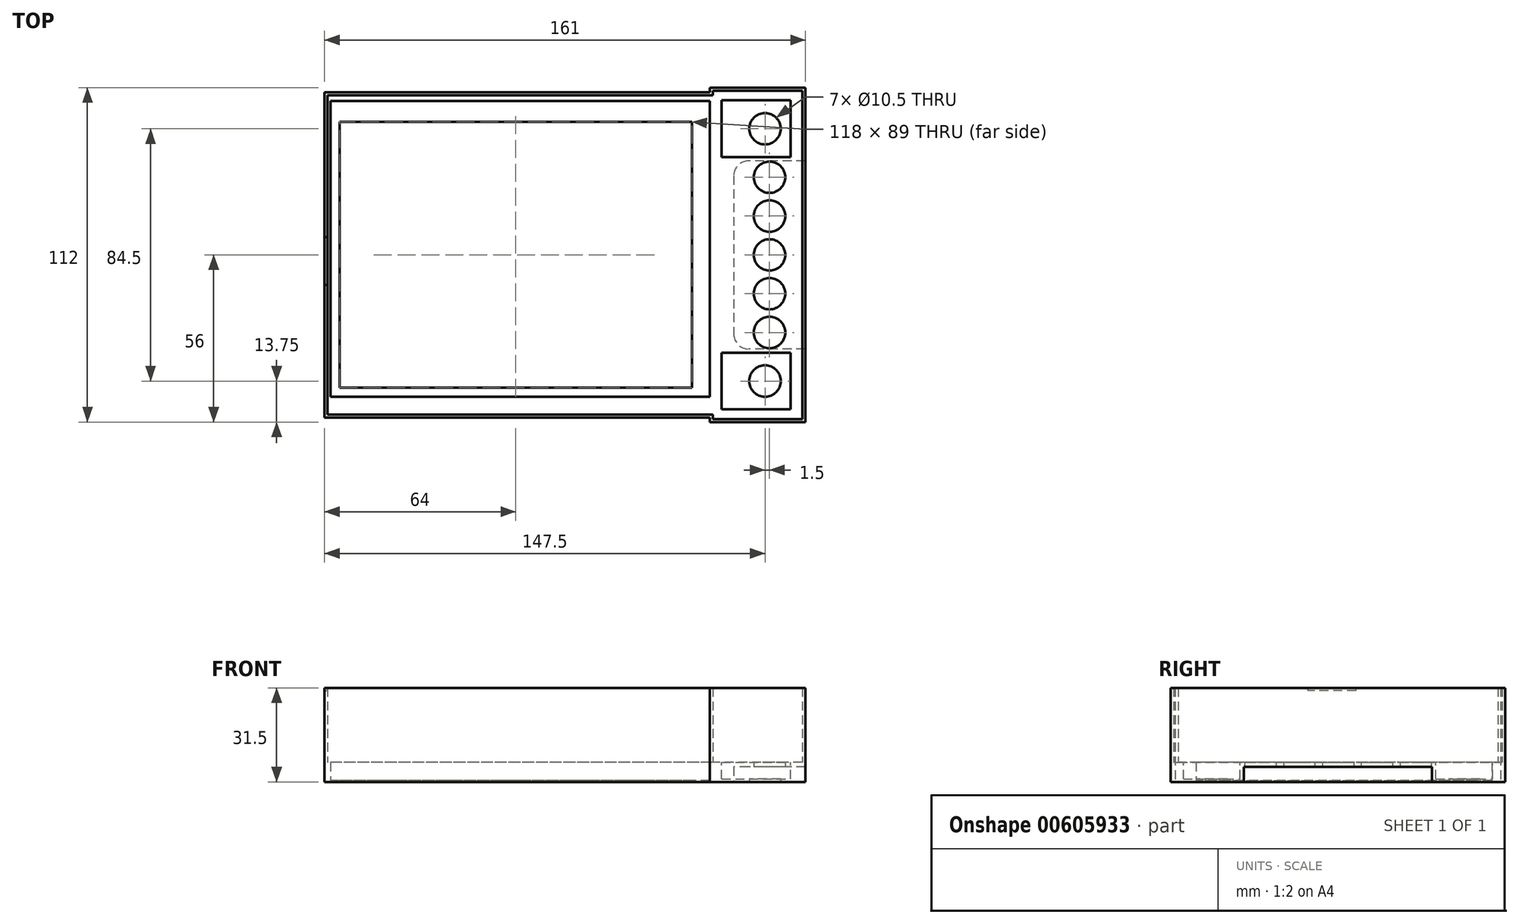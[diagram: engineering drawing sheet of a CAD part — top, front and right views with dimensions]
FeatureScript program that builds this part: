
annotation { "Feature Type Name" : "Feature", "Feature Type Description" : "" }
export const myFeature = defineFeature(function(context is Context, id is Id, definition is map)
    precondition{}
    {
        {
            var Q0;
            Q0=qCreatedBy(makeId("Top.planeOp"),FACE);
            var sketch = newSketch(context, id + "F0", { "sketchPlane" : qUnion([Q0])});
            skLineSegment(sketch, "E0.bottom", {"start": v(59, -44.5) * mm, "end": v(-59, -44.5) * mm});
            skLineSegment(sketch, "E0.top", {"start": v(59, 44.5) * mm, "end": v(-59, 44.5) * mm});
            skLineSegment(sketch, "E0.left", {"start": v(59, -44.5) * mm, "end": v(59, 44.5) * mm});
            skLineSegment(sketch, "E0.right", {"start": v(-59, -44.5) * mm, "end": v(-59, 44.5) * mm});
            skPoint(sketch, "E0.middle", {"position": v(0, 0) * mm});
            skLineSegment(sketch, "E1", {"start": v(65, 51.5) * mm, "end": v(-62, 51.5) * mm});
            skLineSegment(sketch, "E2", {"start": v(-62, 51.5) * mm, "end": v(-62, -47.5) * mm});
            skLineSegment(sketch, "E3", {"start": v(-62, -47.5) * mm, "end": v(65, -47.5) * mm});
            skLineSegment(sketch, "E4", {"start": v(65, 56) * mm, "end": v(97, 56) * mm});
            skLineSegment(sketch, "E5", {"start": v(97, 56) * mm, "end": v(97, -56) * mm});
            skLineSegment(sketch, "E6", {"start": v(97, -56) * mm, "end": v(65, -56) * mm});
            skLineSegment(sketch, "E7", {"start": v(65, 51.5) * mm, "end": v(65, -47.5) * mm});
            skLineSegment(sketch, "E8", {"start": v(65, 56) * mm, "end": v(65, 54.5) * mm});
            skLineSegment(sketch, "E9", {"start": v(65, 54.5) * mm, "end": v(-64, 54.5) * mm});
            skLineSegment(sketch, "E10", {"start": v(-64, 54.5) * mm, "end": v(-64, -54.5) * mm});
            skLineSegment(sketch, "E11", {"start": v(-64, -54.5) * mm, "end": v(65, -54.5) * mm});
            skLineSegment(sketch, "E12", {"start": v(65, -54.5) * mm, "end": v(65, -56) * mm});
            skSolve(sketch);
        }
        {
            var Q0;
            Q0=makeQuery(id+"F0.imprint","IMPRINT",FACE,{"disambiguationData":[TD([[makeQuery(id+"F0.imprint","IMPRINT",EDGE,{"derivedFrom":sQuery(id+"F0.wireOp",EDGE,"E1")}),-1.0]])]});
            var sketch = newSketch(context, id + "F1", { "sketchPlane" : qUnion([Q0])});
            skLineSegment(sketch, "E13", {"start": v(-84.5, 0) * mm, "end": v(108.61, 0) * mm, "construction": true});
            skCircle(sketch, "E14", {"center": v(83.5, -42.25) * mm, "radius": 5.25 * mm});
            skCircle(sketch, "E15", {"center": v(83.5, 42.25) * mm, "radius": 5.25 * mm});
            skCircle(sketch, "E16", {"center": v(85, -26) * mm, "radius": 5.25 * mm});
            skCircle(sketch, "E17", {"center": v(85, -13) * mm, "radius": 5.25 * mm});
            skCircle(sketch, "E18", {"center": v(85, 0) * mm, "radius": 5.25 * mm});
            skCircle(sketch, "E19", {"center": v(85, 13) * mm, "radius": 5.25 * mm});
            skCircle(sketch, "E20", {"center": v(85, 26) * mm, "radius": 5.25 * mm});
            skLineSegment(sketch, "E21", {"start": v(83.5, -71.08) * mm, "end": v(83.5, 74.69) * mm, "construction": true});
            skLineSegment(sketch, "E22", {"start": v(85, -66.88) * mm, "end": v(85, 79.26) * mm, "construction": true});
            skSolve(sketch);
        }
        {
            var Q0;
            Q0=makeQuery(id+"F0.imprint","IMPRINT",FACE,{"disambiguationData":[TD([[makeQuery(id+"F0.imprint","IMPRINT",EDGE,{"derivedFrom":sQuery(id+"F0.wireOp",EDGE,"E1")}),-1.0]])]});
            extrude(context, id + "F2", {"entities" : qUnion([Q0]), "depth" : 6.5 * mm, "offsetDistance" : 25 * mm});
        }
        {
            var Q0;
            Q0=makeQuery(id+"F0.imprint","IMPRINT",FACE,{"disambiguationData":[TD([[makeQuery(id+"F0.imprint","IMPRINT",EDGE,{"derivedFrom":sQuery(id+"F0.wireOp",EDGE,"E0.bottom")}),1.0]])]});
            extrude(context, id + "F3", {"entities" : qUnion([Q0]), "operationType" : NewBodyOperationType.ADD, "depth" : 0.5 * mm, "offsetDistance" : 25 * mm});
        }
        {
            var Q0;
            Q0=makeQuery(id+"F2.opExtrude","CAP_FACE",FACE,{"disambiguationData":[OSD([sQuery(id+"F0.wireOp",EDGE,"E1"),sQuery(id+"F0.wireOp",EDGE,"E2"),sQuery(id+"F0.wireOp",EDGE,"E3"),sQuery(id+"F0.wireOp",EDGE,"E4"),sQuery(id+"F0.wireOp",EDGE,"E5"),sQuery(id+"F0.wireOp",EDGE,"E6"),sQuery(id+"F0.wireOp",EDGE,"E7"),sQuery(id+"F0.wireOp",EDGE,"E8"),sQuery(id+"F0.wireOp",EDGE,"E9"),sQuery(id+"F0.wireOp",EDGE,"E10"),sQuery(id+"F0.wireOp",EDGE,"E11"),sQuery(id+"F0.wireOp",EDGE,"E12")])],"isStart":false});
            var sketch = newSketch(context, id + "F4", { "sketchPlane" : qUnion([Q0])});
            skLineSegment(sketch, "E23", {"start": v(-63, 53.5) * mm, "end": v(66, 53.5) * mm});
            skLineSegment(sketch, "E24", {"start": v(66, 53.5) * mm, "end": v(66, 55) * mm});
            skLineSegment(sketch, "E25", {"start": v(66, 55) * mm, "end": v(96, 55) * mm});
            skLineSegment(sketch, "E26", {"start": v(96, 55) * mm, "end": v(96, -55) * mm});
            skLineSegment(sketch, "E27", {"start": v(96, -55) * mm, "end": v(66, -55) * mm});
            skLineSegment(sketch, "E28", {"start": v(66, -55) * mm, "end": v(66, -53.5) * mm});
            skLineSegment(sketch, "E29", {"start": v(66, -53.5) * mm, "end": v(-63, -53.5) * mm});
            skLineSegment(sketch, "E30", {"start": v(-63, -53.5) * mm, "end": v(-63, 53.5) * mm});
            skSolve(sketch);
        }
        {
            var Q0;
            Q0=makeQuery(id+"F4.imprint","IMPRINT",FACE,{"disambiguationData":[TD([[makeQuery(id+"F4.imprint","IMPRINT",EDGE,{"derivedFrom":sQuery(id+"F4.wireOp",EDGE,"E23")}),1.0]])]});
            extrude(context, id + "F5", {"entities" : qUnion([Q0]), "operationType" : NewBodyOperationType.ADD, "depth" : 25 * mm, "offsetDistance" : 25 * mm});
        }
        {
            var Q0;
            Q0 = qSketchRegion(id + "F1", true);
            extrude(context, id + "F6", {"entities" : qUnion([Q0]), "operationType" : NewBodyOperationType.REMOVE, "endBound" : BoundingType.UP_TO_NEXT, "depth" : 25 * mm, "offsetDistance" : 25 * mm});
        }
        {
            var Q0;
            Q0=makeQuery(id+"F2.opExtrude","CAP_FACE",FACE,{"disambiguationData":[OSD([sQuery(id+"F0.wireOp",EDGE,"E1"),sQuery(id+"F0.wireOp",EDGE,"E2"),sQuery(id+"F0.wireOp",EDGE,"E3"),sQuery(id+"F0.wireOp",EDGE,"E4"),sQuery(id+"F0.wireOp",EDGE,"E5"),sQuery(id+"F0.wireOp",EDGE,"E6"),sQuery(id+"F0.wireOp",EDGE,"E7"),sQuery(id+"F0.wireOp",EDGE,"E8"),sQuery(id+"F0.wireOp",EDGE,"E9"),sQuery(id+"F0.wireOp",EDGE,"E10"),sQuery(id+"F0.wireOp",EDGE,"E11"),sQuery(id+"F0.wireOp",EDGE,"E12")])],"isStart":false});
            var sketch = newSketch(context, id + "F7", { "sketchPlane" : qUnion([Q0])});
            skLineSegment(sketch, "E31.bottom", {"start": v(92, 32.75) * mm, "end": v(75, 32.75) * mm});
            skLineSegment(sketch, "E31.top", {"start": v(92, 51.75) * mm, "end": v(75, 51.75) * mm});
            skLineSegment(sketch, "E31.left", {"start": v(92, 32.75) * mm, "end": v(92, 51.75) * mm});
            skLineSegment(sketch, "E31.right", {"start": v(75, 32.75) * mm, "end": v(75, 51.75) * mm});
            skPoint(sketch, "E31.middle", {"position": v(83.5, 42.25) * mm});
            skLineSegment(sketch, "E32", {"start": v(75, 51.75) * mm, "end": v(69, 51.75) * mm});
            skLineSegment(sketch, "E33", {"start": v(69, 51.75) * mm, "end": v(69, 32.75) * mm});
            skLineSegment(sketch, "E34", {"start": v(69, 32.75) * mm, "end": v(75, 32.75) * mm});
            skLineSegment(sketch, "E35.bottom", {"start": v(92, -51.75) * mm, "end": v(75, -51.75) * mm});
            skLineSegment(sketch, "E35.top", {"start": v(92, -32.75) * mm, "end": v(75, -32.75) * mm});
            skLineSegment(sketch, "E35.left", {"start": v(92, -51.75) * mm, "end": v(92, -32.75) * mm});
            skLineSegment(sketch, "E35.right", {"start": v(75, -51.75) * mm, "end": v(75, -32.75) * mm});
            skPoint(sketch, "E35.middle", {"position": v(83.5, -42.25) * mm});
            skLineSegment(sketch, "E36", {"start": v(75, -32.75) * mm, "end": v(69, -32.75) * mm});
            skLineSegment(sketch, "E37", {"start": v(69, -32.75) * mm, "end": v(69, -51.75) * mm});
            skLineSegment(sketch, "E38", {"start": v(69, -51.75) * mm, "end": v(75, -51.75) * mm});
            skSolve(sketch);
        }
        {
            var Q0;
            Q0=makeQuery(id+"F7.imprint","IMPRINT",FACE,{"disambiguationData":[TD([[makeQuery(id+"F7.imprint","IMPRINT",EDGE,{"derivedFrom":sQuery(id+"F7.wireOp",EDGE,"E31.right")}),1.0]])]});
            var Q1;
            Q1=makeQuery(id+"F7.imprint","IMPRINT",FACE,{"disambiguationData":[TD([[makeQuery(id+"F7.imprint","IMPRINT",EDGE,{"derivedFrom":sQuery(id+"F7.wireOp",EDGE,"E31.bottom")}),-1.0]])]});
            var Q2;
            Q2=makeQuery(id+"F7.imprint","IMPRINT",FACE,{"disambiguationData":[TD([[makeQuery(id+"F7.imprint","IMPRINT",EDGE,{"derivedFrom":sQuery(id+"F7.wireOp",EDGE,"E35.right")}),1.0]])]});
            var Q3;
            Q3=makeQuery(id+"F7.imprint","IMPRINT",FACE,{"disambiguationData":[TD([[makeQuery(id+"F7.imprint","IMPRINT",EDGE,{"derivedFrom":sQuery(id+"F7.wireOp",EDGE,"E35.bottom")}),-1.0]])]});
            extrude(context, id + "F8", {"entities" : qUnion([Q0, Q1, Q2, Q3]), "operationType" : NewBodyOperationType.REMOVE, "oppositeDirection" : true, "depth" : 5.5 * mm, "offsetDistance" : 25 * mm});
        }
        {
            var Q0;
            Q0=makeQuery(id+"F0.imprint","IMPRINT",FACE,{"disambiguationData":[TD([[makeQuery(id+"F0.imprint","IMPRINT",EDGE,{"derivedFrom":sQuery(id+"F0.wireOp",EDGE,"E1")}),-1.0]])]});
            var sketch = newSketch(context, id + "F9", { "sketchPlane" : qUnion([Q0])});
            skCircle(sketch, "E39.0", {"center": v(85, 0) * mm, "radius": 5.25 * mm});
            skLineSegment(sketch, "E40.bottom", {"start": v(97, 31.5) * mm, "end": v(78, 31.5) * mm});
            skLineSegment(sketch, "E40.top", {"start": v(97, -31.5) * mm, "end": v(78, -31.5) * mm});
            skLineSegment(sketch, "E40.left", {"start": v(97, 31.5) * mm, "end": v(97, -31.5) * mm});
            skLineSegment(sketch, "E40.right", {"start": v(73, 26.5) * mm, "end": v(73, -26.5) * mm});
            skPoint(sketch, "E41.visualSharp", {"position": v(73, -31.5) * mm});
            skArc(sketch, "E41.filletArc", {"start": v(73, -26.5) * mm, "mid": v(74.46, -30.04) * mm, "end": v(78, -31.5) * mm});
            skPoint(sketch, "E42.visualSharp", {"position": v(73, 31.5) * mm});
            skArc(sketch, "E42.filletArc", {"start": v(78, 31.5) * mm, "mid": v(74.46, 30.04) * mm, "end": v(73, 26.5) * mm});
            skSolve(sketch);
        }
        {
            var Q0;
            Q0 = qSketchRegion(id + "F9", true);
            extrude(context, id + "F10", {"entities" : qUnion([Q0]), "operationType" : NewBodyOperationType.REMOVE, "depth" : 5 * mm, "offsetDistance" : 25 * mm});
        }
        {
            var Q0;
            Q0=makeQuery(id+"F5.opExtrude","CAP_FACE",FACE,{"disambiguationData":[OSD([sQuery(id+"F0.wireOp",EDGE,"E4"),sQuery(id+"F0.wireOp",EDGE,"E5"),sQuery(id+"F0.wireOp",EDGE,"E6"),sQuery(id+"F0.wireOp",EDGE,"E8"),sQuery(id+"F0.wireOp",EDGE,"E9"),sQuery(id+"F0.wireOp",EDGE,"E10"),sQuery(id+"F0.wireOp",EDGE,"E11"),sQuery(id+"F0.wireOp",EDGE,"E12"),sQuery(id+"F4.wireOp",EDGE,"E23"),sQuery(id+"F4.wireOp",EDGE,"E24"),sQuery(id+"F4.wireOp",EDGE,"E25"),sQuery(id+"F4.wireOp",EDGE,"E26"),sQuery(id+"F4.wireOp",EDGE,"E27"),sQuery(id+"F4.wireOp",EDGE,"E28"),sQuery(id+"F4.wireOp",EDGE,"E29"),sQuery(id+"F4.wireOp",EDGE,"E30")])],"isStart":false});
            var sketch = newSketch(context, id + "F11", { "sketchPlane" : qUnion([Q0])});
            skLineSegment(sketch, "E43.bottom", {"start": v(-64, -10) * mm, "end": v(-63, -10) * mm});
            skLineSegment(sketch, "E43.top", {"start": v(-64, 6) * mm, "end": v(-63, 6) * mm});
            skLineSegment(sketch, "E43.left", {"start": v(-64, -10) * mm, "end": v(-64, 6) * mm});
            skLineSegment(sketch, "E43.right", {"start": v(-63, -10) * mm, "end": v(-63, 6) * mm});
            skSolve(sketch);
        }
        {
            var Q0;
            Q0=makeQuery(id+"F11.imprint","IMPRINT",FACE,{"disambiguationData":[TD([[makeQuery(id+"F11.imprint","IMPRINT",EDGE,{"derivedFrom":sQuery(id+"F11.wireOp",EDGE,"E43.bottom")}),1.0]])]});
            extrude(context, id + "F12", {"entities" : qUnion([Q0]), "operationType" : NewBodyOperationType.REMOVE, "oppositeDirection" : true, "depth" : 1 * mm, "offsetDistance" : 25 * mm});
        }
    });
